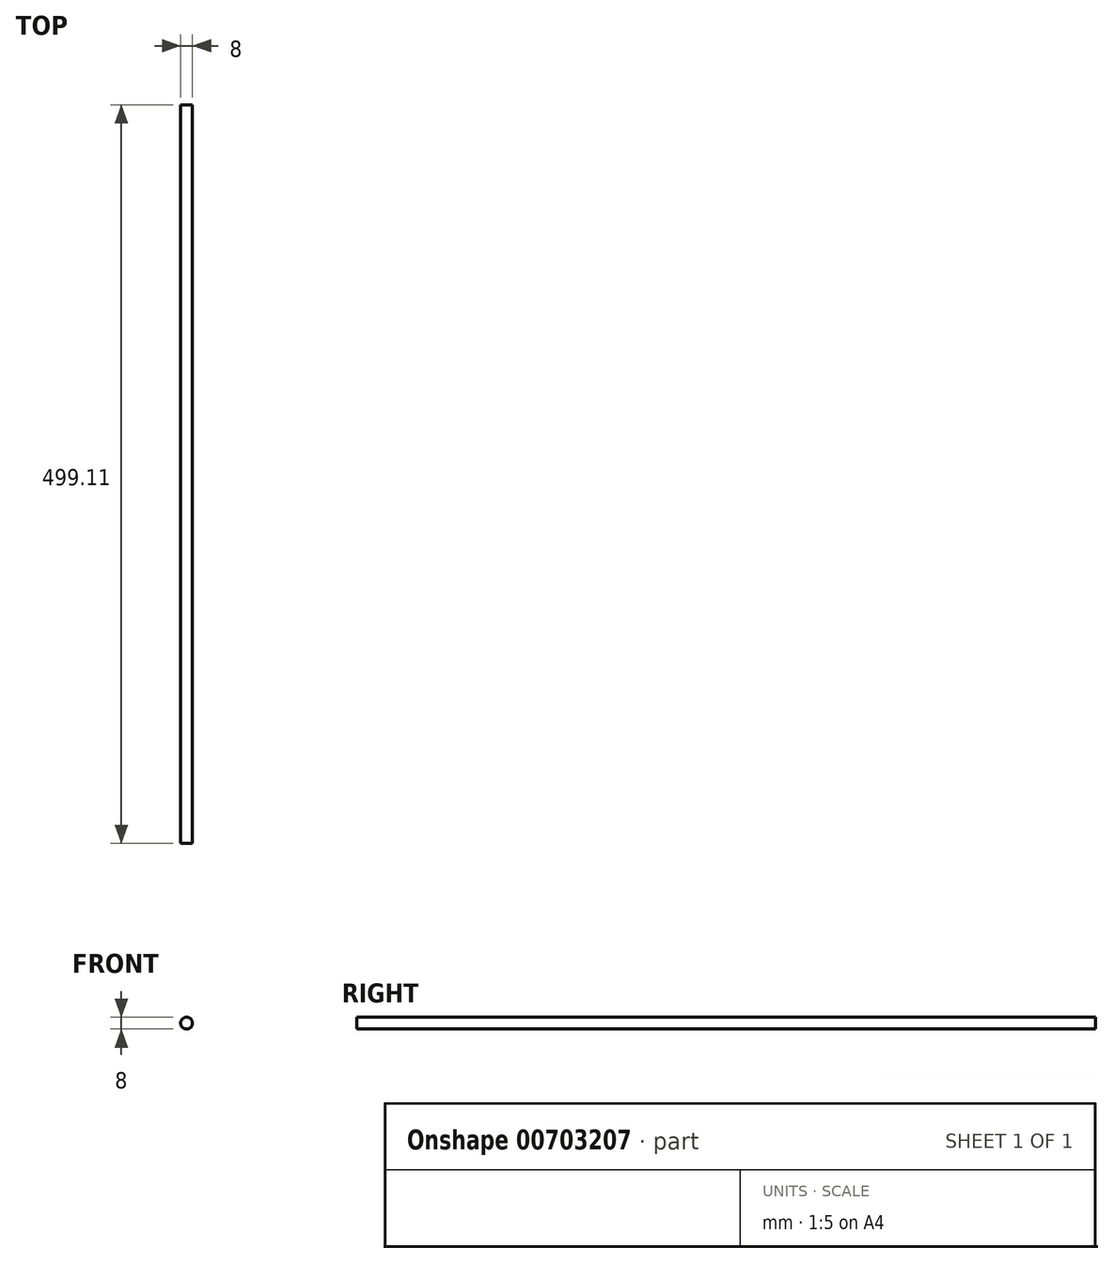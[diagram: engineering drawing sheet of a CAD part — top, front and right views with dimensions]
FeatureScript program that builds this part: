
annotation { "Feature Type Name" : "Feature", "Feature Type Description" : "" }
export const myFeature = defineFeature(function(context is Context, id is Id, definition is map)
    precondition{}
    {
        {
            var Q0;
            Q0=qCreatedBy(makeId("Front.planeOp"),FACE);
            var sketch = newSketch(context, id + "F0", { "sketchPlane" : qUnion([Q0])});
            skCircle(sketch, "E0", {"center": v(0, 0) * mm, "radius": 4 * mm});
            skSolve(sketch);
        }
        {
            var Q0;
            Q0 = qSketchRegion(id + "F0", true);
            extrude(context, id + "F1", {"entities" : qUnion([Q0]), "depth" : 499.1 * mm, "offsetDistance" : 25.4 * mm});
        }
    });
